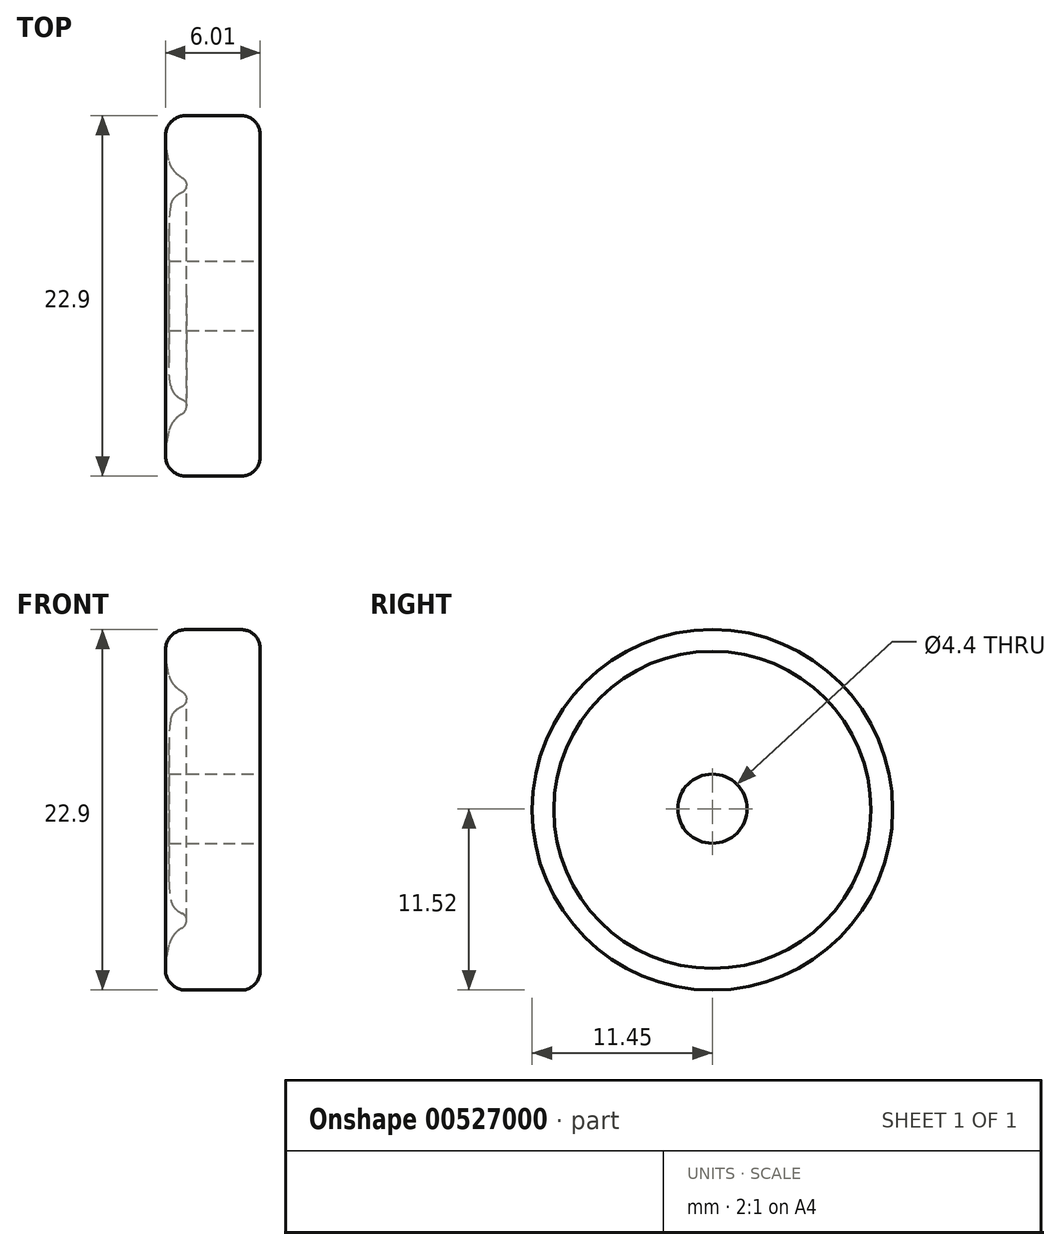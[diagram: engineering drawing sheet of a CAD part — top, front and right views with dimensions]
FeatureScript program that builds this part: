
annotation { "Feature Type Name" : "Feature", "Feature Type Description" : "" }
export const myFeature = defineFeature(function(context is Context, id is Id, definition is map)
    precondition{}
    {
        {
            var Q0;
            Q0=qCreatedBy(makeId("Front.planeOp"),FACE);
            var sketch = newSketch(context, id + "F0", { "sketchPlane" : qUnion([Q0])});
            skLineSegment(sketch, "E0", {"start": v(-6, 0) * mm, "end": v(-5.77, 0) * mm});
            skLineSegment(sketch, "E1", {"start": v(0, 0) * mm, "end": v(0, 10) * mm});
            skLineSegment(sketch, "E2", {"start": v(-6, 10) * mm, "end": v(-6, 0) * mm, "construction": true});
            skLineSegment(sketch, "E3", {"start": v(-6, 10) * mm, "end": v(0, 10) * mm, "construction": true});
            skArc(sketch, "E4", {"start": v(-4.7, 11.38) * mm, "mid": v(-5.65, 10.97) * mm, "end": v(-6, 10) * mm});
            skLineSegment(sketch, "E5", {"start": v(-4.7, 11.38) * mm, "end": v(-1.2, 11.38) * mm});
            skPoint(sketch, "E6.center.orphan", {"position": v(-1.5, 10) * mm});
            skArc(sketch, "E7", {"start": v(-1.2, 11.38) * mm, "mid": v(-0.28, 10.96) * mm, "end": v(0, 10) * mm});
            skArc(sketch, "E8", {"start": v(-6, 10) * mm, "mid": v(-5.92, 9.25) * mm, "end": v(-5.77, 8.5) * mm});
            skArc(sketch, "E9", {"start": v(-5.77, 8.5) * mm, "mid": v(-5.63, 8.13) * mm, "end": v(-5.4, 7.8) * mm});
            skArc(sketch, "E10", {"start": v(-5.4, 7.8) * mm, "mid": v(-5.2, 7.6) * mm, "end": v(-4.97, 7.45) * mm});
            skArc(sketch, "E11", {"start": v(-4.97, 7.45) * mm, "mid": v(-4.74, 7.23) * mm, "end": v(-4.66, 6.93) * mm});
            skArc(sketch, "E12", {"start": v(-4.66, 6.93) * mm, "mid": v(-4.73, 6.67) * mm, "end": v(-4.94, 6.5) * mm});
            skArc(sketch, "E13", {"start": v(-4.94, 6.5) * mm, "mid": v(-5.17, 6.38) * mm, "end": v(-5.37, 6.22) * mm});
            skArc(sketch, "E14", {"start": v(-5.37, 6.22) * mm, "mid": v(-5.55, 5.97) * mm, "end": v(-5.66, 5.67) * mm});
            skArc(sketch, "E15", {"start": v(-5.66, 5.67) * mm, "mid": v(-5.74, 5.1) * mm, "end": v(-5.77, 4.5) * mm});
            skArc(sketch, "E16", {"start": v(-5.77, 4.5) * mm, "mid": v(-5.77, 2.25) * mm, "end": v(-5.77, 0) * mm});
            skPoint(sketch, "E17.orphan", {"position": v(-46.27, 0) * mm});
            skLineSegment(sketch, "E18", {"start": v(-5.77, 0) * mm, "end": v(-6, 0) * mm});
            skPoint(sketch, "E18.startSnap0", {"position": v(-2.89, 0) * mm});
            skPoint(sketch, "E19.orphan", {"position": v(4.46, 0) * mm});
            skLineSegment(sketch, "E20", {"start": v(0, 0) * mm, "end": v(-5.77, 0) * mm});
            skLineSegment(sketch, "E21", {"start": v(2.17, -0.07) * mm, "end": v(-6.88, -0.07) * mm});
            skSolve(sketch);
        }
        {
            var Q0;
            Q0=makeQuery(id+"F0.imprint","IMPRINT",FACE,{"disambiguationData":[TD([[makeQuery(id+"F0.imprint","IMPRINT",EDGE,{"derivedFrom":sQuery(id+"F0.wireOp",EDGE,"E1")}),1.0]])]});
            var Q1;
            Q1=sQuery(id+"F0.wireOp",EDGE,"E21");
            revolve(context, id + "F1", {"entities" : qUnion([Q0]), "axis" : qUnion([Q1]), "revolveType" : RevolveType.FULL});
        }
        {
            var Q0;
            Q0=makeQuery(id+"F1.opRevolve","SWEPT_FACE",FACE,{"disambiguationData":[OSD([sQuery(id+"F0.wireOp",EDGE,"E1")])]});
            var sketch = newSketch(context, id + "F2", { "sketchPlane" : qUnion([Q0])});
            skCircle(sketch, "E22", {"center": v(0, 0) * mm, "radius": 2.2 * mm});
            skSolve(sketch);
        }
        {
            var Q0;
            Q0=makeQuery(id+"F2.imprint","IMPRINT",FACE,{"disambiguationData":[TD([[makeQuery(id+"F2.imprint","IMPRINT",EDGE,{"derivedFrom":sQuery(id+"F2.wireOp",EDGE,"E22")}),1.0]])]});
            extrude(context, id + "F3", {"entities" : qUnion([Q0]), "operationType" : NewBodyOperationType.REMOVE, "oppositeDirection" : true, "depth" : 25 * mm, "offsetDistance" : 25 * mm});
        }
    });
